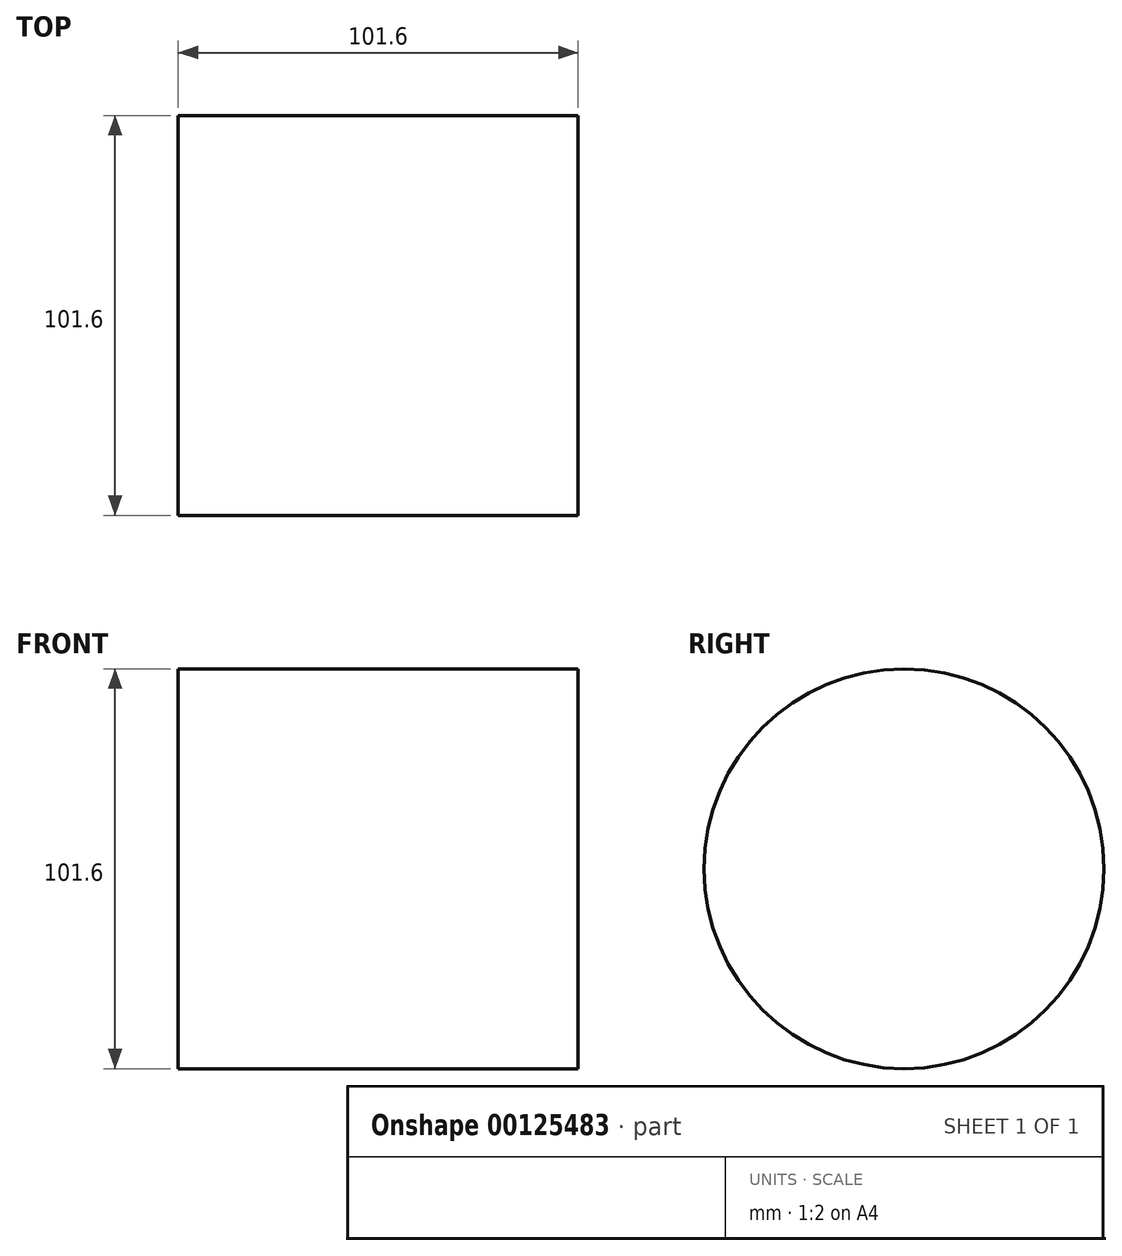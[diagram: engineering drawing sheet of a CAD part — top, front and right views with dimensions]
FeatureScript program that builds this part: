
annotation { "Feature Type Name" : "Feature", "Feature Type Description" : "" }
export const myFeature = defineFeature(function(context is Context, id is Id, definition is map)
    precondition{}
    {
        {
            var Q0;
            Q0=qCreatedBy(makeId("Front.planeOp"),FACE);
            var sketch = newSketch(context, id + "F0", { "sketchPlane" : qUnion([Q0])});
            skLineSegment(sketch, "E0.bottom", {"start": v(50.8, -25.4) * mm, "end": v(-50.8, -25.4) * mm});
            skLineSegment(sketch, "E0.top", {"start": v(50.8, 25.4) * mm, "end": v(-50.8, 25.4) * mm});
            skLineSegment(sketch, "E0.left", {"start": v(50.8, -25.4) * mm, "end": v(50.8, 25.4) * mm});
            skLineSegment(sketch, "E0.right", {"start": v(-50.8, -25.4) * mm, "end": v(-50.8, 25.4) * mm});
            skPoint(sketch, "E0.middle", {"position": v(0, 0) * mm});
            skSolve(sketch);
        }
        {
            var Q0;
            Q0 = qSketchRegion(id + "F0", true);
            var Q1;
            Q1=sQuery(id+"F0.wireOp",EDGE,"E0.bottom");
            revolve(context, id + "F1", {"entities" : qUnion([Q0]), "axis" : qUnion([Q1]), "revolveType" : RevolveType.FULL});
        }
    });
